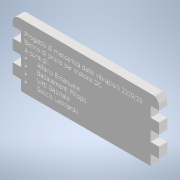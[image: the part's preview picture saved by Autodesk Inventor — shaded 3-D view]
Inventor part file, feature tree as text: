
AUTODESK INVENTOR PART (.ipt)
format: ipt  version: 2020.2 (Build 242310000, 310)  size: 2,935,808 bytes
history: native  units: mm
features: extrude x3, sketch x3
ambient origin geometry x8: Origin, YZ Plane, XZ Plane, XY Plane, X Axis, Y Axis, Z Axis, Center Point
bodies: Solido1 (feature_tree)
feature tree (6):
  extrude  "Estrusione1"  Depth=70.0mm
  extrude  "Estrusione2"  Depth=30.0mm
  extrude  "Estrusione3"  Depth=4.0mm TaperAngle=0.0deg
  sketch  "Schizzo1"
  sketch  "Schizzo2"
  sketch  "Schizzo3"
